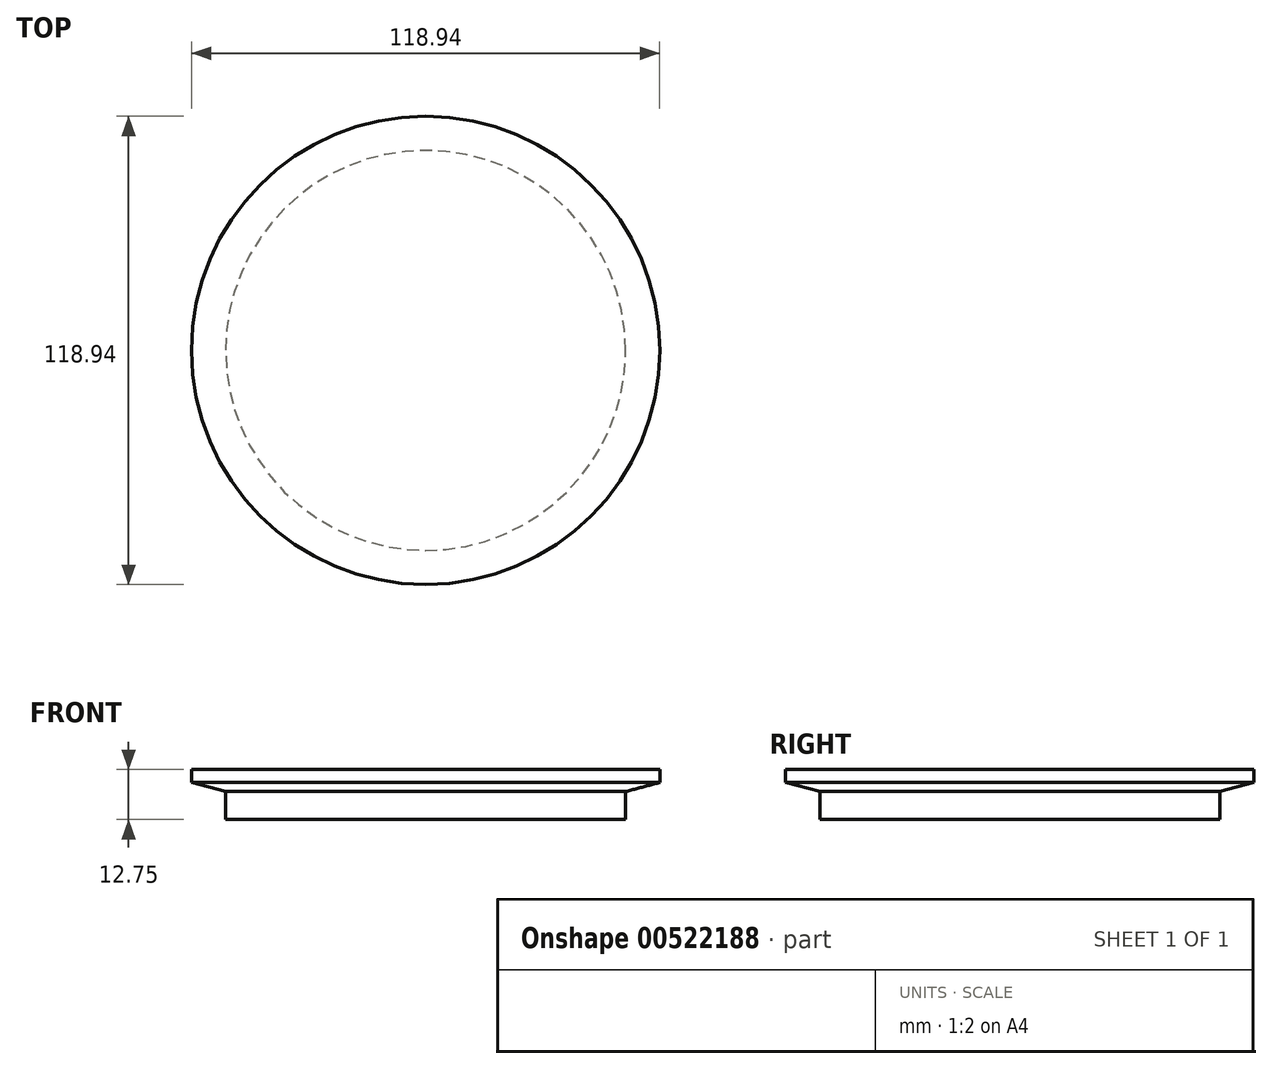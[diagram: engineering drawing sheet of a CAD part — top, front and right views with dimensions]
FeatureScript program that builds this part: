
annotation { "Feature Type Name" : "Feature", "Feature Type Description" : "" }
export const myFeature = defineFeature(function(context is Context, id is Id, definition is map)
    precondition{}
    {
        {
            var Q0;
            Q0=qCreatedBy(makeId("Front.planeOp"),FACE);
            var sketch = newSketch(context, id + "F0", { "sketchPlane" : qUnion([Q0])});
            skLineSegment(sketch, "E0", {"start": v(0, 0) * mm, "end": v(0, 85.37) * mm, "construction": true});
            skLineSegment(sketch, "E1", {"start": v(0, 0) * mm, "end": v(0, -83.14) * mm, "construction": true});
            skLineSegment(sketch, "E2", {"start": v(0, 0) * mm, "end": v(59.47, 0) * mm});
            skLineSegment(sketch, "E3", {"start": v(59.47, 0) * mm, "end": v(59.47, -3.3) * mm});
            skLineSegment(sketch, "E4", {"start": v(59.47, -3.3) * mm, "end": v(50.8, -5.63) * mm});
            skLineSegment(sketch, "E5", {"start": v(0, 0) * mm, "end": v(0, -12.75) * mm});
            skLineSegment(sketch, "E6", {"start": v(0, -12.75) * mm, "end": v(50.8, -12.75) * mm});
            skLineSegment(sketch, "E7", {"start": v(50.8, -12.75) * mm, "end": v(50.8, -5.63) * mm});
            skSolve(sketch);
        }
        {
            var Q0;
            Q0=makeQuery(id+"F0.imprint","IMPRINT",FACE,{"disambiguationData":[TD([[makeQuery(id+"F0.imprint","IMPRINT",EDGE,{"derivedFrom":sQuery(id+"F0.wireOp",EDGE,"E2")}),-1.0]])]});
            var Q1;
            Q1=sQuery(id+"F0.wireOp",EDGE,"E5");
            revolve(context, id + "F1", {"entities" : qUnion([Q0]), "axis" : qUnion([Q1]), "revolveType" : RevolveType.FULL});
        }
    });
